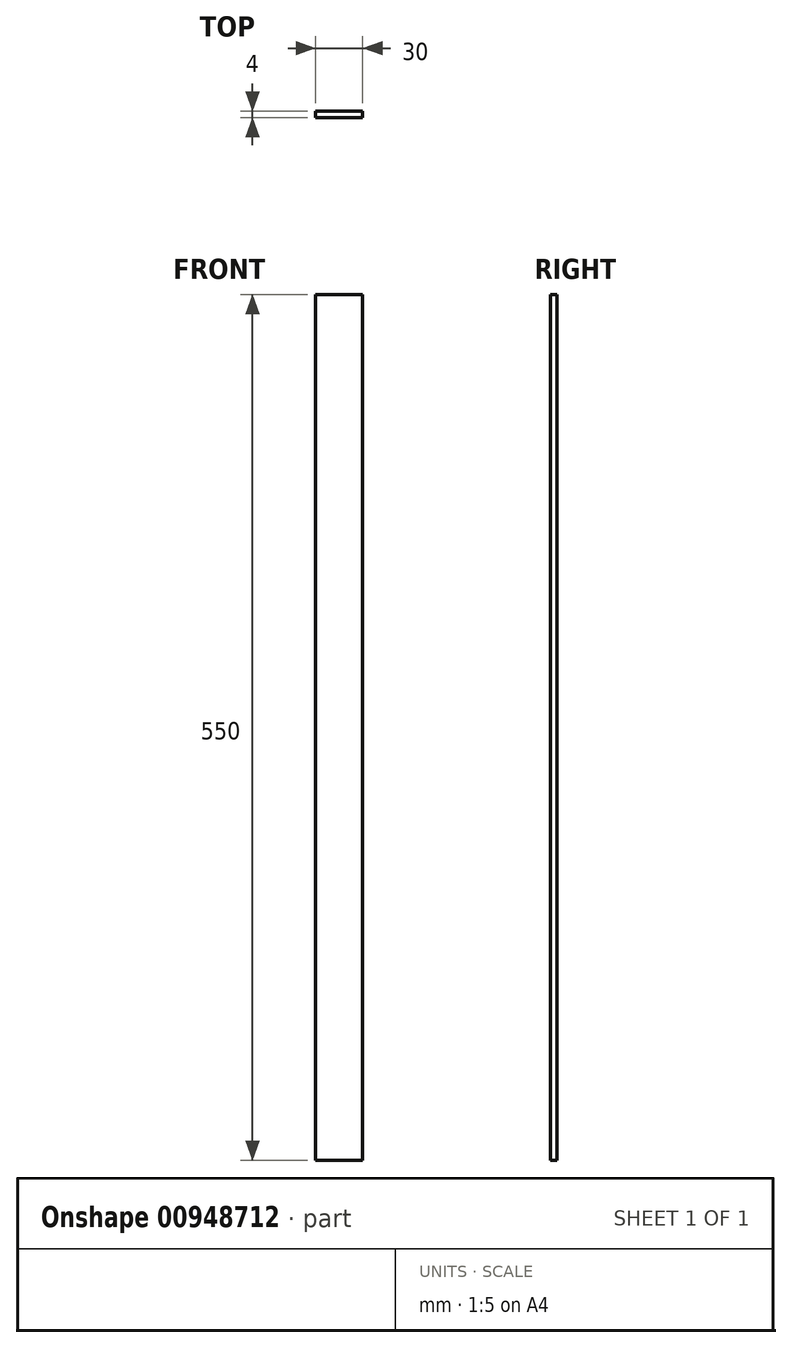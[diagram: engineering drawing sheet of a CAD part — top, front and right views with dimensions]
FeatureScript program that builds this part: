
annotation { "Feature Type Name" : "Feature", "Feature Type Description" : "" }
export const myFeature = defineFeature(function(context is Context, id is Id, definition is map)
    precondition{}
    {
        {
            var Q0;
            Q0=qCreatedBy(makeId("Front.planeOp"),FACE);
            var sketch = newSketch(context, id + "F0", { "sketchPlane" : qUnion([Q0])});
            skLineSegment(sketch, "E0.bottom", {"start": v(-79.02, 273.26) * mm, "end": v(-49.02, 273.26) * mm});
            skLineSegment(sketch, "E0.top", {"start": v(-79.02, -276.74) * mm, "end": v(-49.02, -276.74) * mm});
            skLineSegment(sketch, "E0.left", {"start": v(-79.02, 273.26) * mm, "end": v(-79.02, -276.74) * mm});
            skLineSegment(sketch, "E0.right", {"start": v(-49.02, 273.26) * mm, "end": v(-49.02, -276.74) * mm});
            skSolve(sketch);
        }
        {
            var Q0;
            Q0 = qSketchRegion(id + "F0", true);
            extrude(context, id + "F1", {"entities" : qUnion([Q0]), "depth" : 4 * mm, "offsetDistance" : 25 * mm});
        }
    });
